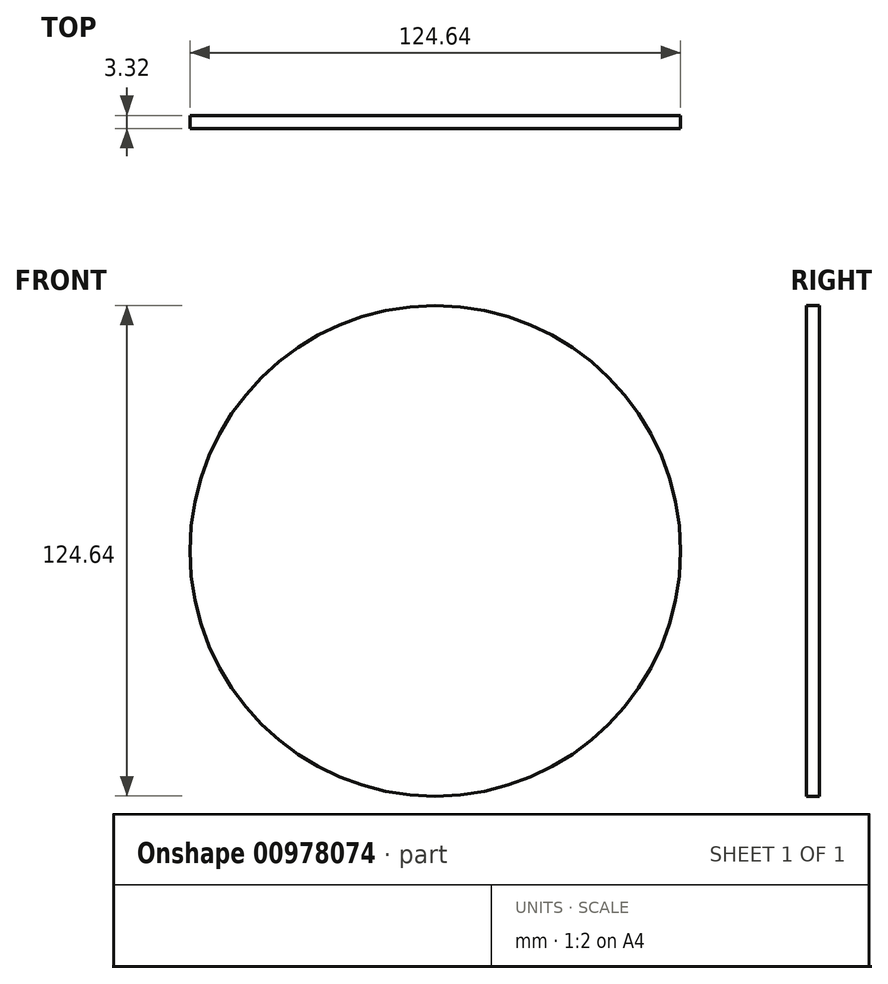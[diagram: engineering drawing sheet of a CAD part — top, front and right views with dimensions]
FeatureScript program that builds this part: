
annotation { "Feature Type Name" : "Feature", "Feature Type Description" : "" }
export const myFeature = defineFeature(function(context is Context, id is Id, definition is map)
    precondition{}
    {
        {
            var Q0;
            Q0=qCreatedBy(makeId("Front.planeOp"),FACE);
            var sketch = newSketch(context, id + "F0", { "sketchPlane" : qUnion([Q0])});
            skCircle(sketch, "E0", {"center": v(0, 0) * mm, "radius": 62.32 * mm});
            skSolve(sketch);
        }
        {
            var Q0;
            Q0=makeQuery(id+"F0.imprint","IMPRINT",FACE,{"disambiguationData":[TD([[makeQuery(id+"F0.imprint","IMPRINT",EDGE,{"derivedFrom":sQuery(id+"F0.wireOp",EDGE,"E0")}),1.0]])]});
            extrude(context, id + "F1", {"entities" : qUnion([Q0]), "depth" : 3.32 * mm, "offsetDistance" : 25.4 * mm});
        }
    });
